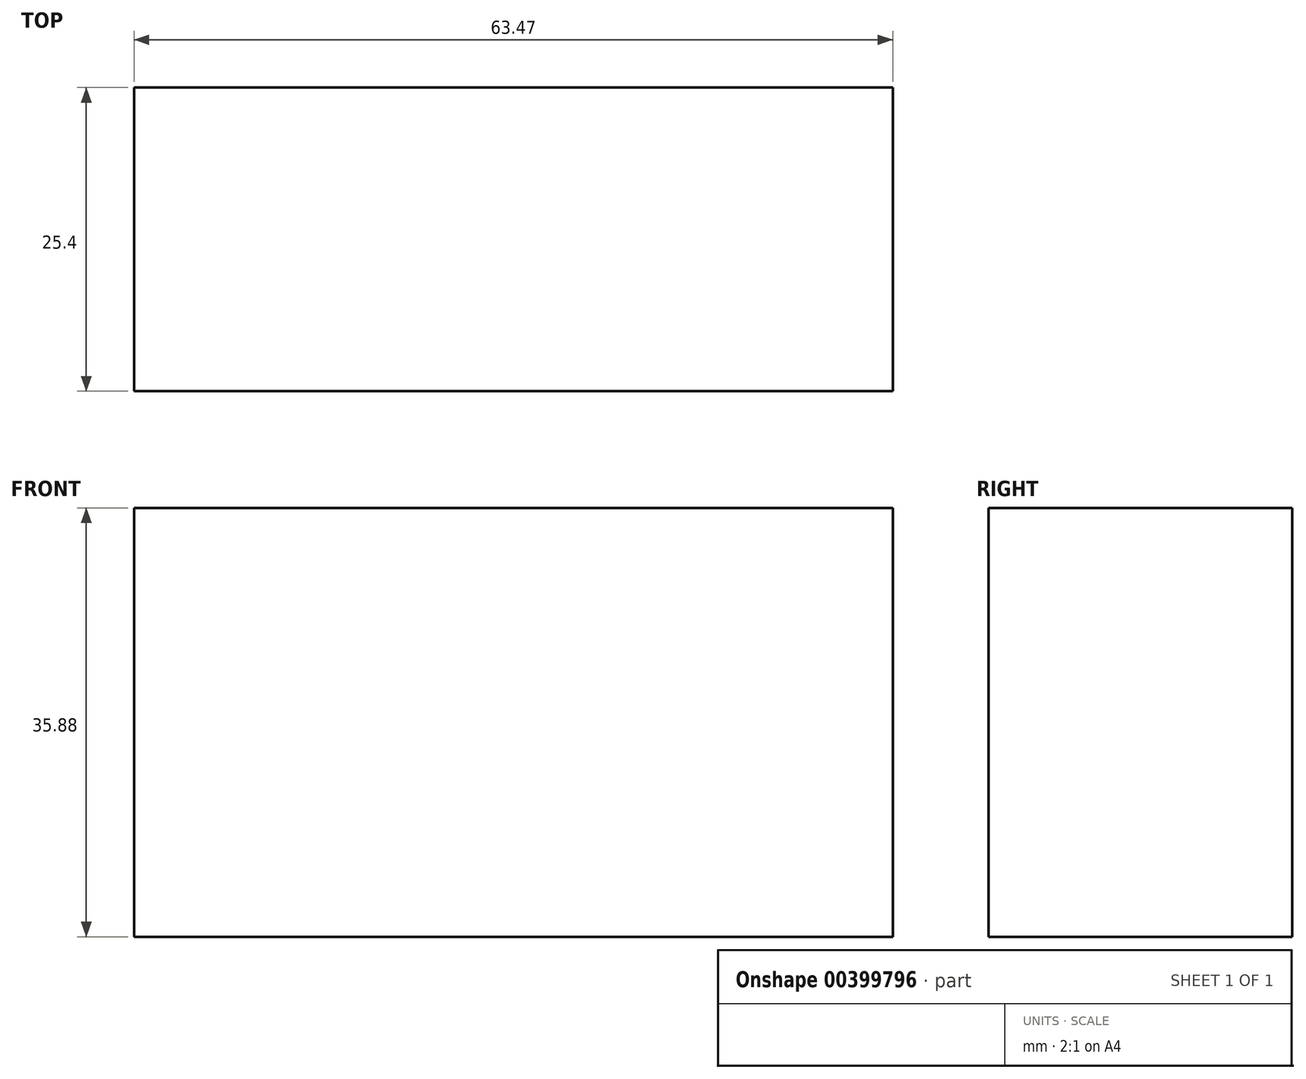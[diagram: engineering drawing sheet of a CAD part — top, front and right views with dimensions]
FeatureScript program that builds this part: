
annotation { "Feature Type Name" : "Feature", "Feature Type Description" : "" }
export const myFeature = defineFeature(function(context is Context, id is Id, definition is map)
    precondition{}
    {
        {
            var Q0;
            Q0=qCreatedBy(makeId("Front.planeOp"),FACE);
            var sketch = newSketch(context, id + "F0", { "sketchPlane" : qUnion([Q0])});
            skLineSegment(sketch, "E0.bottom", {"start": v(-31.36, 18.82) * mm, "end": v(32.11, 18.82) * mm});
            skLineSegment(sketch, "E0.top", {"start": v(-31.36, -17.06) * mm, "end": v(32.11, -17.06) * mm});
            skLineSegment(sketch, "E0.left", {"start": v(-31.36, 18.82) * mm, "end": v(-31.36, -17.06) * mm});
            skLineSegment(sketch, "E0.right", {"start": v(32.11, 18.82) * mm, "end": v(32.11, -17.06) * mm});
            skLineSegment(sketch, "E1.bottom", {"start": v(32.11, 18.82) * mm, "end": v(51.34, 18.82) * mm});
            skLineSegment(sketch, "E1.top", {"start": v(32.11, -17.06) * mm, "end": v(51.34, -17.06) * mm});
            skLineSegment(sketch, "E1.right", {"start": v(51.34, 18.82) * mm, "end": v(51.34, -17.06) * mm});
            skSolve(sketch);
        }
        {
            var Q0;
            Q0=makeQuery(id+"F0.imprint","IMPRINT",FACE,{"disambiguationData":[TD([[makeQuery(id+"F0.imprint","IMPRINT",EDGE,{"derivedFrom":sQuery(id+"F0.wireOp",EDGE,"E0.bottom")}),-1.0]])]});
            extrude(context, id + "F1", {"entities" : qUnion([Q0]), "depth" : 25.4 * mm});
        }
    });
